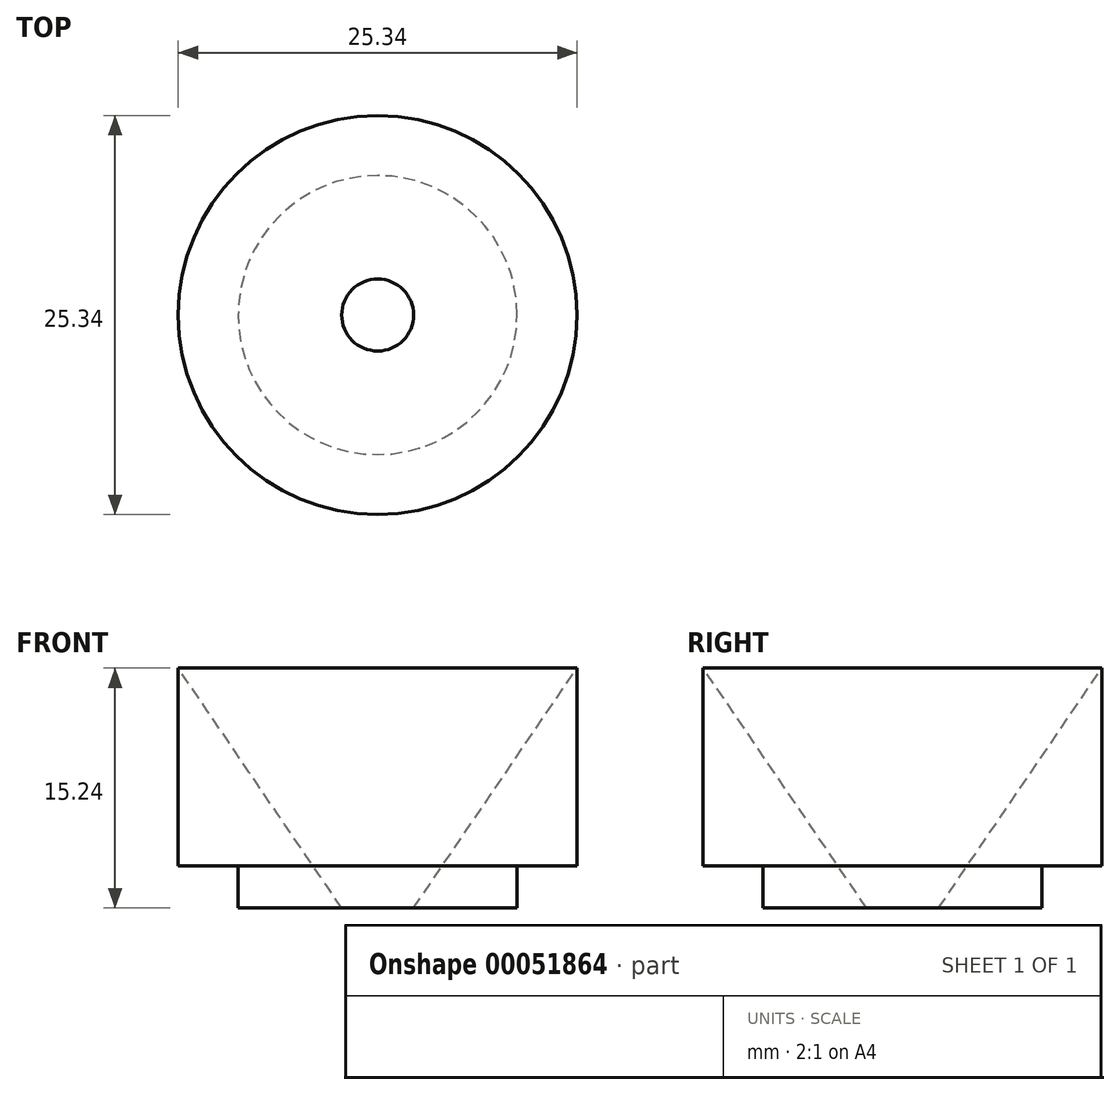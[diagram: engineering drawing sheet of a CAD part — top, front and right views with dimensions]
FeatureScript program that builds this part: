
annotation { "Feature Type Name" : "Feature", "Feature Type Description" : "" }
export const myFeature = defineFeature(function(context is Context, id is Id, definition is map)
    precondition{}
    {
        {
            var Q0;
            Q0=qCreatedBy(makeId("Front.planeOp"),FACE);
            var sketch = newSketch(context, id + "F0", { "sketchPlane" : qUnion([Q0])});
            skLineSegment(sketch, "E0", {"start": v(2.29, 0) * mm, "end": v(12.67, 15.24) * mm});
            skLineSegment(sketch, "E1", {"start": v(12.67, 15.24) * mm, "end": v(12.67, 2.67) * mm});
            skLineSegment(sketch, "E2", {"start": v(8.86, 0) * mm, "end": v(2.29, 0) * mm});
            skLineSegment(sketch, "E3", {"start": v(0, 0) * mm, "end": v(0, 14.1) * mm, "construction": true});
            skLineSegment(sketch, "E4", {"start": v(8.86, 0) * mm, "end": v(8.86, 2.67) * mm});
            skLineSegment(sketch, "E5", {"start": v(8.86, 2.67) * mm, "end": v(12.67, 2.67) * mm});
            skPoint(sketch, "E6.orphan", {"position": v(12.67, 0) * mm});
            skSolve(sketch);
        }
        {
            var Q0;
            Q0=qSketchRegion(id+"F0",true);
            var Q1;
            Q1=sQuery(id+"F0.wireOp",EDGE,"E3");
            revolve(context, id + "F1", {"entities" : qUnion([Q0]), "axis" : qUnion([Q1]), "revolveType" : RevolveType.FULL});
        }
    });
